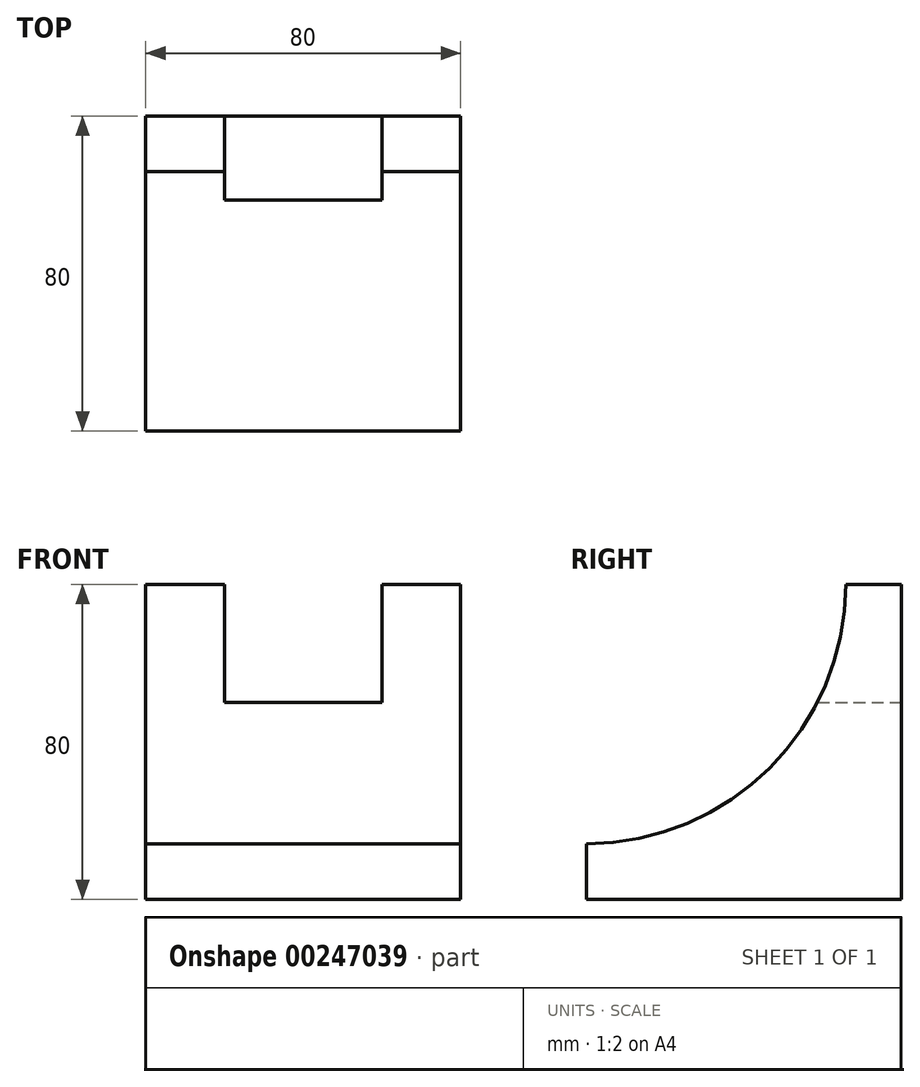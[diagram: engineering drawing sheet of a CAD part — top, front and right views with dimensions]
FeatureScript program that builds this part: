
annotation { "Feature Type Name" : "Feature", "Feature Type Description" : "" }
export const myFeature = defineFeature(function(context is Context, id is Id, definition is map)
    precondition{}
    {
        {
            var Q0;
            Q0=qCreatedBy(makeId("Front.planeOp"),FACE);
            var sketch = newSketch(context, id + "F0", { "sketchPlane" : qUnion([Q0])});
            skLineSegment(sketch, "E0", {"start": v(-41.58, 48.52) * mm, "end": v(-41.58, -31.48) * mm});
            skLineSegment(sketch, "E1", {"start": v(-41.58, -31.48) * mm, "end": v(38.42, -31.48) * mm});
            skLineSegment(sketch, "E2", {"start": v(38.42, -31.48) * mm, "end": v(38.42, 48.52) * mm});
            skLineSegment(sketch, "E3", {"start": v(38.42, 48.52) * mm, "end": v(18.42, 48.52) * mm});
            skLineSegment(sketch, "E4", {"start": v(-21.58, 48.52) * mm, "end": v(-21.58, 18.52) * mm});
            skLineSegment(sketch, "E5", {"start": v(-21.58, 18.52) * mm, "end": v(18.42, 18.52) * mm});
            skLineSegment(sketch, "E6", {"start": v(18.42, 18.52) * mm, "end": v(18.42, 48.52) * mm});
            skLineSegment(sketch, "E7.trimOffspring", {"start": v(-21.58, 48.52) * mm, "end": v(-41.58, 48.52) * mm});
            skSolve(sketch);
        }
        {
            var Q0;
            Q0=makeQuery(id+"F0.imprint","IMPRINT",FACE,{"disambiguationData":[TD([[makeQuery(id+"F0.imprint","IMPRINT",EDGE,{"derivedFrom":sQuery(id+"F0.wireOp",EDGE,"E0")}),1.0]])]});
            extrude(context, id + "F1", {"entities" : qUnion([Q0]), "endBound" : BoundingType.SYMMETRIC, "depth" : 80 * mm});
        }
        {
            var Q0;
            Q0=makeQuery(id+"F1.opExtrude","SWEPT_FACE",FACE,{"disambiguationData":[OSD([sQuery(id+"F0.wireOp",EDGE,"E0")])]});
            var sketch = newSketch(context, id + "F2", { "sketchPlane" : qUnion([Q0])});
            skPoint(sketch, "E8", {"position": v(-25.87, 48.52) * mm});
            skPoint(sketch, "E9", {"position": v(40, -15.58) * mm});
            skLineSegment(sketch, "E10", {"start": v(55.18, -15.58) * mm, "end": v(40, -15.58) * mm});
            skLineSegment(sketch, "E11", {"start": v(-25.87, 48.52) * mm, "end": v(-25.87, 48.52) * mm});
            skArc(sketch, "E12", {"start": v(-25.87, 48.52) * mm, "mid": v(-0.86, -3.15) * mm, "end": v(55.18, -15.58) * mm});
            skLineSegment(sketch, "E13", {"start": v(-25.87, 48.52) * mm, "end": v(40, 48.52) * mm});
            skLineSegment(sketch, "E14", {"start": v(40, 48.52) * mm, "end": v(40, -15.58) * mm});
            skSolve(sketch);
        }
        {
            var Q0;
            {var subQ0=sQuery(id+"F2.wireOp",EDGE,"E13");Q0=makeQuery(id+"F2.imprint","IMPRINT",FACE,{"disambiguationData":[TD([[makeQuery(id+"F2.imprint","IMPRINT",EDGE,{"derivedFrom":subQ0}),1.0]])]});}
            extrude(context, id + "F3", {"entities" : qUnion([Q0]), "operationType" : NewBodyOperationType.REMOVE, "endBound" : BoundingType.THROUGH_ALL, "oppositeDirection" : true, "depth" : 25 * mm});
        }
    });
